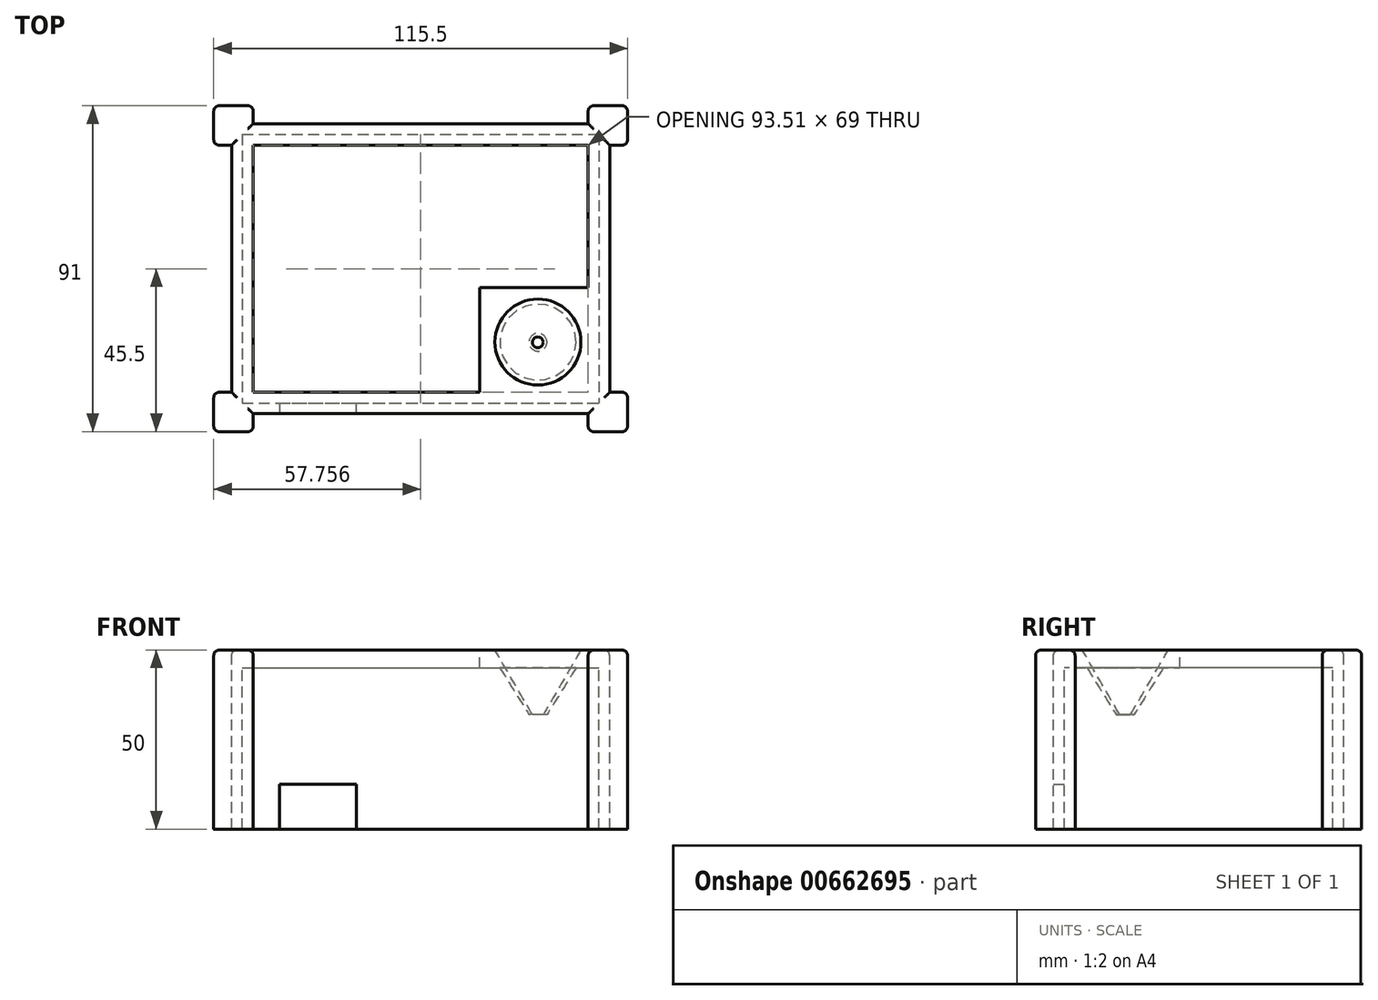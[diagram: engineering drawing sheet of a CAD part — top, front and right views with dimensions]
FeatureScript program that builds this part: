
annotation { "Feature Type Name" : "Feature", "Feature Type Description" : "" }
export const myFeature = defineFeature(function(context is Context, id is Id, definition is map)
    precondition{}
    {
        {
            var Q0;
            Q0=qCreatedBy(makeId("Top.planeOp"),FACE);
            var sketch = newSketch(context, id + "F0", { "sketchPlane" : qUnion([Q0])});
            skLineSegment(sketch, "E0.bottom", {"start": v(0, 0) * mm, "end": v(199, 0) * mm});
            skLineSegment(sketch, "E0.top", {"start": v(0, 150) * mm, "end": v(199, 150) * mm});
            skLineSegment(sketch, "E0.left", {"start": v(0, 0) * mm, "end": v(0, 150) * mm});
            skLineSegment(sketch, "E0.right", {"start": v(199, 0) * mm, "end": v(199, 150) * mm});
            skLineSegment(sketch, "E1.bottom", {"start": v(6, 6) * mm, "end": v(193.02, 6) * mm});
            skLineSegment(sketch, "E1.top", {"start": v(6, 144) * mm, "end": v(193.02, 144) * mm});
            skLineSegment(sketch, "E1.left", {"start": v(6, 6) * mm, "end": v(6, 144) * mm});
            skLineSegment(sketch, "E1.right", {"start": v(193.02, 6) * mm, "end": v(193.02, 144) * mm});
            skCircle(sketch, "E2", {"center": v(165, 116) * mm, "radius": 27.5 * mm});
            skLineSegment(sketch, "E3", {"start": v(132.43, 144) * mm, "end": v(132.43, 85.49) * mm});
            skLineSegment(sketch, "E4", {"start": v(132.43, 85.49) * mm, "end": v(193.02, 85.49) * mm});
            skLineSegment(sketch, "E5.bottom", {"start": v(6, -6) * mm, "end": v(193.02, -6) * mm});
            skLineSegment(sketch, "E5.top", {"start": v(6, 156) * mm, "end": v(193.02, 156) * mm});
            skLineSegment(sketch, "E5.left", {"start": v(-6, 6) * mm, "end": v(-6, 144) * mm});
            skLineSegment(sketch, "E5.right", {"start": v(205, 6) * mm, "end": v(205, 144) * mm});
            skLineSegment(sketch, "E6", {"start": v(-6, 144) * mm, "end": v(-16, 144) * mm});
            skLineSegment(sketch, "E7", {"start": v(-16, 144) * mm, "end": v(-16, 166) * mm});
            skLineSegment(sketch, "E8", {"start": v(-16, 166) * mm, "end": v(6, 166) * mm});
            skLineSegment(sketch, "E9", {"start": v(6, 166) * mm, "end": v(6, 156) * mm});
            skLineSegment(sketch, "E10", {"start": v(-6, 6) * mm, "end": v(-16, 6) * mm});
            skLineSegment(sketch, "E11", {"start": v(6, -6) * mm, "end": v(6, -16) * mm});
            skLineSegment(sketch, "E12", {"start": v(6, -16) * mm, "end": v(-16, -16) * mm});
            skLineSegment(sketch, "E13", {"start": v(-16, -16) * mm, "end": v(-16, 6) * mm});
            skLineSegment(sketch, "E14", {"start": v(193.02, -6) * mm, "end": v(193.02, -16) * mm});
            skLineSegment(sketch, "E15", {"start": v(205, 6) * mm, "end": v(215, 6) * mm});
            skLineSegment(sketch, "E16", {"start": v(215, 6) * mm, "end": v(215, -16) * mm});
            skLineSegment(sketch, "E17", {"start": v(215, -16) * mm, "end": v(193.02, -16) * mm});
            skLineSegment(sketch, "E18", {"start": v(193.02, 156) * mm, "end": v(193.02, 166) * mm});
            skLineSegment(sketch, "E19", {"start": v(205, 144) * mm, "end": v(215, 144) * mm});
            skLineSegment(sketch, "E20", {"start": v(215, 144) * mm, "end": v(215, 166) * mm});
            skLineSegment(sketch, "E21", {"start": v(215, 166) * mm, "end": v(193.02, 166) * mm});
            skPoint(sketch, "E22.orphan", {"position": v(-6, -6) * mm});
            skLineSegment(sketch, "E23", {"start": v(20.74, 150) * mm, "end": v(20.74, 156) * mm});
            skLineSegment(sketch, "E24", {"start": v(63.63, 156) * mm, "end": v(63.63, 150) * mm});
            skSolve(sketch);
        }
        {
            var Q0;
            Q0=qCreatedBy(makeId("Top.planeOp"),FACE);
            cPlane(context, id + "F1", {"entities" : qUnion([Q0]), "cplaneType" : CPlaneType.OFFSET, "offset" : 36 * mm, "width" : 150 * mm, "height" : 150 * mm});
        }
        {
            var Q0;
            Q0=qCreatedBy(makeId("Top.planeOp"),FACE);
            cPlane(context, id + "F2", {"entities" : qUnion([Q0]), "cplaneType" : CPlaneType.OFFSET, "offset" : 10 * mm, "width" : 150 * mm, "height" : 150 * mm});
        }
        {
            var Q0;
            Q0=makeQuery(id+"F0.imprint","IMPRINT",FACE,{"disambiguationData":[TD([[makeQuery(id+"F0.imprint","IMPRINT",EDGE,{"derivedFrom":sQuery(id+"F0.wireOp",EDGE,"E2")}),1.0]])]});
            var Q1;
            Q1=makeQuery(id+"F0.imprint","IMPRINT",FACE,{"disambiguationData":[TD([[makeQuery(id+"F0.imprint","IMPRINT",EDGE,{"derivedFrom":sQuery(id+"F0.wireOp",EDGE,"E2")}),-1.0]])]});
            extrude(context, id + "F3", {"entities" : qUnion([Q0, Q1]), "depth" : 10 * mm, "offsetDistance" : 25 * mm});
        }
        {
            var Q0;
            Q0=qCreatedBy(id+"F1.planeOp",FACE);
            var sketch = newSketch(context, id + "F4", { "sketchPlane" : qUnion([Q0])});
            skCircle(sketch, "E25", {"center": v(165.01, 116.06) * mm, "radius": 5 * mm});
            skSolve(sketch);
        }
        {
            var Q1;
            Q1=makeQuery(id+"F4.imprint","IMPRINT",FACE,{"disambiguationData":[TD([[makeQuery(id+"F4.imprint","IMPRINT",EDGE,{"derivedFrom":sQuery(id+"F4.wireOp",EDGE,"E25")}),1.0]])]});
            var Q2;
            Q2=makeQuery(id+"F0.imprint","IMPRINT",FACE,{"disambiguationData":[TD([[makeQuery(id+"F0.imprint","IMPRINT",EDGE,{"derivedFrom":sQuery(id+"F0.wireOp",EDGE,"E2")}),1.0]])]});
            loft(context, id + "F5", {"operationType" : NewBodyOperationType.ADD, "sheetProfilesArray" : [{ "sheetProfileEntities" : qUnion([Q1]) }, { "sheetProfileEntities" : qUnion([Q2]) }]});
        }
        {
            var Q0;
            Q0=qCreatedBy(makeId("Top.planeOp"),FACE);
            var sketch = newSketch(context, id + "F6", { "sketchPlane" : qUnion([Q0])});
            skCircle(sketch, "E26", {"center": v(164.99, 115.94) * mm, "radius": 24 * mm});
            skSolve(sketch);
        }
        {
            var Q0;
            Q0=qCreatedBy(id+"F1.planeOp",FACE);
            var sketch = newSketch(context, id + "F7", { "sketchPlane" : qUnion([Q0])});
            skCircle(sketch, "E27", {"center": v(164.92, 116.08) * mm, "radius": 3 * mm});
            skSolve(sketch);
        }
        {
            var Q1;
            Q1=makeQuery(id+"F6.imprint","IMPRINT",FACE,{"disambiguationData":[TD([[makeQuery(id+"F6.imprint","IMPRINT",EDGE,{"derivedFrom":sQuery(id+"F6.wireOp",EDGE,"E26")}),1.0]])]});
            var Q2;
            Q2=makeQuery(id+"F7.imprint","IMPRINT",FACE,{"disambiguationData":[TD([[makeQuery(id+"F7.imprint","IMPRINT",EDGE,{"derivedFrom":sQuery(id+"F7.wireOp",EDGE,"E27")}),1.0]])]});
            loft(context, id + "F8", {"operationType" : NewBodyOperationType.REMOVE, "sheetProfilesArray" : [{ "sheetProfileEntities" : qUnion([Q1]) }, { "sheetProfileEntities" : qUnion([Q2]) }]});
        }
        {
            var Q0;
            Q0=makeQuery(id+"F0.imprint","IMPRINT",FACE,{"disambiguationData":[TD([[makeQuery(id+"F0.imprint","IMPRINT",EDGE,{"derivedFrom":sQuery(id+"F0.wireOp",EDGE,"E0.bottom")}),1.0]])]});
            extrude(context, id + "F9", {"entities" : qUnion([Q0]), "operationType" : NewBodyOperationType.ADD, "depth" : 10 * mm, "offsetDistance" : 25 * mm});
        }
        {
            var Q0;
            Q0=makeQuery(id+"F0.imprint","IMPRINT",FACE,{"disambiguationData":[TD([[makeQuery(id+"F0.imprint","IMPRINT",EDGE,{"derivedFrom":sQuery(id+"F0.wireOp",EDGE,"E0.bottom")}),-1.0]])]});
            extrude(context, id + "F10", {"entities" : qUnion([Q0]), "operationType" : NewBodyOperationType.ADD, "depth" : 100 * mm, "offsetDistance" : 25 * mm});
        }
        {
            var Q0;
            {var subQ0=sQuery(id+"F0.wireOp",EDGE,"E23");Q0=makeQuery(id+"F0.imprint","IMPRINT",FACE,{"disambiguationData":[TD([[makeQuery(id+"F0.imprint","IMPRINT",EDGE,{"derivedFrom":subQ0}),-1.0]])]});}
            extrude(context, id + "F11", {"entities" : qUnion([Q0]), "operationType" : NewBodyOperationType.ADD, "depth" : 75 * mm, "offsetDistance" : 25 * mm});
        }
        {
            var Q0;
            Q0=makeQuery(id+"F10.opExtrude","CAP_EDGE",EDGE,{"disambiguationData":[OSD([sQuery(id+"F0.wireOp",EDGE,"E17")])],"isStart":true});
            var Q1;
            Q1=makeQuery(id+"F10.opExtrude","CAP_EDGE",EDGE,{"disambiguationData":[OSD([sQuery(id+"F0.wireOp",EDGE,"E16")])],"isStart":true});
            var Q2;
            Q2=makeQuery(id+"F10.opExtrude","CAP_EDGE",EDGE,{"disambiguationData":[OSD([sQuery(id+"F0.wireOp",EDGE,"E5.right")])],"isStart":true});
            var Q3;
            Q3=makeQuery(id+"F10.opExtrude","CAP_EDGE",EDGE,{"disambiguationData":[OSD([sQuery(id+"F0.wireOp",EDGE,"E15")])],"isStart":true});
            var Q4;
            Q4=makeQuery(id+"F10.opExtrude","CAP_EDGE",EDGE,{"disambiguationData":[OSD([sQuery(id+"F0.wireOp",EDGE,"E19")])],"isStart":true});
            var Q5;
            Q5=makeQuery(id+"F10.opExtrude","CAP_EDGE",EDGE,{"disambiguationData":[OSD([sQuery(id+"F0.wireOp",EDGE,"E20")])],"isStart":true});
            var Q6;
            Q6=makeQuery(id+"F10.opExtrude","CAP_EDGE",EDGE,{"disambiguationData":[OSD([sQuery(id+"F0.wireOp",EDGE,"E21")])],"isStart":true});
            var Q7;
            Q7=makeQuery(id+"F10.opExtrude","CAP_EDGE",EDGE,{"disambiguationData":[OSD([sQuery(id+"F0.wireOp",EDGE,"E18")])],"isStart":true});
            var Q8;
            Q8=makeQuery(id+"F10.opExtrude","CAP_EDGE",EDGE,{"disambiguationData":[OSD([sQuery(id+"F0.wireOp",EDGE,"E5.top")])],"isStart":true});
            var Q9;
            Q9=makeQuery(id+"F10.opExtrude","CAP_EDGE",EDGE,{"disambiguationData":[OSD([sQuery(id+"F0.wireOp",EDGE,"E8")])],"isStart":true});
            var Q10;
            Q10=makeQuery(id+"F10.opExtrude","CAP_EDGE",EDGE,{"disambiguationData":[OSD([sQuery(id+"F0.wireOp",EDGE,"E9")])],"isStart":true});
            var Q11;
            Q11=makeQuery(id+"F10.opExtrude","CAP_EDGE",EDGE,{"disambiguationData":[OSD([sQuery(id+"F0.wireOp",EDGE,"E7")])],"isStart":true});
            var Q12;
            Q12=makeQuery(id+"F10.opExtrude","CAP_EDGE",EDGE,{"disambiguationData":[OSD([sQuery(id+"F0.wireOp",EDGE,"E6")])],"isStart":true});
            var Q13;
            Q13=makeQuery(id+"F10.opExtrude","CAP_EDGE",EDGE,{"disambiguationData":[OSD([sQuery(id+"F0.wireOp",EDGE,"E5.left")])],"isStart":true});
            var Q14;
            Q14=makeQuery(id+"F10.opExtrude","CAP_EDGE",EDGE,{"disambiguationData":[OSD([sQuery(id+"F0.wireOp",EDGE,"E10")])],"isStart":true});
            var Q15;
            Q15=makeQuery(id+"F10.opExtrude","CAP_EDGE",EDGE,{"disambiguationData":[OSD([sQuery(id+"F0.wireOp",EDGE,"E12")])],"isStart":true});
            var Q16;
            Q16=makeQuery(id+"F10.opExtrude","CAP_EDGE",EDGE,{"disambiguationData":[OSD([sQuery(id+"F0.wireOp",EDGE,"E13")])],"isStart":true});
            var Q17;
            Q17=makeQuery(id+"F10.opExtrude","CAP_EDGE",EDGE,{"disambiguationData":[OSD([sQuery(id+"F0.wireOp",EDGE,"E11")])],"isStart":true});
            var Q18;
            Q18=makeQuery(id+"F10.opExtrude","CAP_EDGE",EDGE,{"disambiguationData":[OSD([sQuery(id+"F0.wireOp",EDGE,"E5.bottom")])],"isStart":true});
            var Q19;
            Q19=makeQuery(id+"F10.opExtrude","CAP_EDGE",EDGE,{"disambiguationData":[OSD([sQuery(id+"F0.wireOp",EDGE,"E14")])],"isStart":true});
            fillet(context, id + "F12", {"entities" : qUnion([Q0, Q1, Q2, Q3, Q4, Q5, Q6, Q7, Q8, Q9, Q10, Q11, Q12, Q13, Q14, Q15, Q16, Q17, Q18, Q19]), "radius" : 3 * mm, "tangentPropagation" : true, "allowEdgeOverflow" : false});
        }
        {
            var Q0;
            Q0=makeQuery(id+"F10.opExtrude","SWEPT_EDGE",EDGE,{"disambiguationData":[OSD([sQuery(id+"F0.wireOp",EDGE,"E16"),sQuery(id+"F0.wireOp",EDGE,"E17")])]});
            var Q1;
            Q1=makeQuery(id+"F10.opExtrude","SWEPT_EDGE",EDGE,{"disambiguationData":[OSD([sQuery(id+"F0.wireOp",EDGE,"E14"),sQuery(id+"F0.wireOp",EDGE,"E17")])]});
            var Q2;
            Q2=makeQuery(id+"F10.opExtrude","SWEPT_EDGE",EDGE,{"disambiguationData":[OSD([sQuery(id+"F0.wireOp",EDGE,"E15"),sQuery(id+"F0.wireOp",EDGE,"E16")])]});
            var Q3;
            Q3=makeQuery(id+"F10.opExtrude","SWEPT_EDGE",EDGE,{"disambiguationData":[OSD([sQuery(id+"F0.wireOp",EDGE,"E19"),sQuery(id+"F0.wireOp",EDGE,"E20")])]});
            var Q4;
            Q4=makeQuery(id+"F10.opExtrude","SWEPT_EDGE",EDGE,{"disambiguationData":[OSD([sQuery(id+"F0.wireOp",EDGE,"E20"),sQuery(id+"F0.wireOp",EDGE,"E21")])]});
            var Q5;
            Q5=makeQuery(id+"F10.opExtrude","SWEPT_EDGE",EDGE,{"disambiguationData":[OSD([sQuery(id+"F0.wireOp",EDGE,"E18"),sQuery(id+"F0.wireOp",EDGE,"E21")])]});
            var Q6;
            Q6=makeQuery(id+"F10.opExtrude","SWEPT_EDGE",EDGE,{"disambiguationData":[OSD([sQuery(id+"F0.wireOp",EDGE,"E11"),sQuery(id+"F0.wireOp",EDGE,"E12")])]});
            var Q7;
            Q7=makeQuery(id+"F10.opExtrude","SWEPT_EDGE",EDGE,{"disambiguationData":[OSD([sQuery(id+"F0.wireOp",EDGE,"E12"),sQuery(id+"F0.wireOp",EDGE,"E13")])]});
            var Q8;
            Q8=makeQuery(id+"F10.opExtrude","SWEPT_EDGE",EDGE,{"disambiguationData":[OSD([sQuery(id+"F0.wireOp",EDGE,"E10"),sQuery(id+"F0.wireOp",EDGE,"E13")])]});
            var Q9;
            Q9=makeQuery(id+"F10.opExtrude","SWEPT_EDGE",EDGE,{"disambiguationData":[OSD([sQuery(id+"F0.wireOp",EDGE,"E6"),sQuery(id+"F0.wireOp",EDGE,"E7")])]});
            var Q10;
            Q10=makeQuery(id+"F10.opExtrude","SWEPT_EDGE",EDGE,{"disambiguationData":[OSD([sQuery(id+"F0.wireOp",EDGE,"E7"),sQuery(id+"F0.wireOp",EDGE,"E8")])]});
            var Q11;
            Q11=makeQuery(id+"F10.opExtrude","SWEPT_EDGE",EDGE,{"disambiguationData":[OSD([sQuery(id+"F0.wireOp",EDGE,"E8"),sQuery(id+"F0.wireOp",EDGE,"E9")])]});
            fillet(context, id + "F13", {"entities" : qUnion([Q0, Q1, Q2, Q3, Q4, Q5, Q6, Q7, Q8, Q9, Q10, Q11]), "radius" : 3 * mm, "tangentPropagation" : true, "allowEdgeOverflow" : false});
        }
        {
            var Q0;
            Q0=makeQuery(id+"F3.opExtrude","SWEPT_BODY",BODY,{"disambiguationData":[OSD([sQuery(id+"F0.wireOp",EDGE,"E1.top"),sQuery(id+"F0.wireOp",EDGE,"E1.right"),sQuery(id+"F0.wireOp",EDGE,"E3"),sQuery(id+"F0.wireOp",EDGE,"E4")])]});
            var Q1;
            Q1=sQuery(id+"F0.wireOp",VERTEX,"E17.start");
            transform(context, id + "F14", {"entities" : qUnion([Q0]), "transformType" : TransformType.SCALE_UNIFORMLY, "scale" : .5, "scalePoint" : qUnion([Q1]), "makeCopy" : false});
        }
        {
            var Q0;
            Q0=makeQuery(id+"F3.opExtrude","SWEPT_BODY",BODY,{"disambiguationData":[OSD([sQuery(id+"F0.wireOp",EDGE,"E1.top"),sQuery(id+"F0.wireOp",EDGE,"E1.right"),sQuery(id+"F0.wireOp",EDGE,"E3"),sQuery(id+"F0.wireOp",EDGE,"E4")])]});
            var Q1;
            Q1=sQuery(id+"F0.wireOp",EDGE,"E5.bottom");
            transform(context, id + "F15", {"entities" : qUnion([Q0]), "transformType" : TransformType.ROTATION, "transformAxis" : qUnion([Q1]), "angle" : 180 * degree, "makeCopy" : false});
        }
    });
